# Revit family: RFll-TY3551_Imperial
name_source: partatom
category: Sprinklers
units: mm (PartAtom-declared; Revit-internal decimal feet)

## family parameters
Always vertical = Yes
Cut with Voids When Loaded = No
Maintain Annotation Orientation = No
OmniClass Number = 23.65.70.17.11.24
OmniClass Title = Fire Fighting Sprinkler Heads
Part Type = Normal
Room Calculation Point = No
Round Connector Dimension = Use Diameter
Shared = No
Work Plane-Based = No

## types (2) — shared parameters
COBie = Yes
COBie.Component.Name = Sprinklers:Concealed Flush
COBie.Type = Yes
COBie.Type.AssetType = Fixed
COBie.Type.Category = Pr_70_55_97_84:Sprinklers
COBie.Type.DurationUnit = year
COBie.Type.Finish = Bronze
COBie.Type.Manufacturer = Tyco Fire Protection Products
COBie.Type.Material = Bronze
COBie.Type.NominalHeight = 0' - 0"
COBie.Type.NominalLength = 0' - 0"
COBie.Type.NominalWidth = 0' - 0"
COBie.Type.Shape = Cylinder
COBie.Type.Size = 1/2"(DN15)
COBie.Type.WarrantyGuarantorParts = http://tycofsbp.com
Cover Plate Color = Tyco - White
Coverage = Standard
Coverage_ = Standard
Default Elevation = 0' - 0"
Finish_ = Natural Brass
K-Factor = 5.6
Manufacturer = Tyco Fire Protection Products
Manufacturer URL = www.tyco-fire.com
Material_ = Bronze
Model = RFII
Nominal Diameter 1 = 1"
Orifice = Extra Large
Orifice Size = 0"
Outside Diameter 1 = 1"
Response = Standard
Response_ = Standard
SIN No = TFP181
Takeout 1 = 2"
zero-valued in all types: COBie.Type.ReplacementCost, Style Id

## per-type parameters (varying)
| type | COBie.Component.Description | COBie.Type.ModelNumber | COBie.Type.ModelReference | Description | Part No | Technical Data Sheet No | Temperature Rating |
| RFll Concealed Pendent 1/2" NPT 155°F Brass_51-790-1-155 | RFII Concealed Flush SC SR 155°F K5.6 1/2 NPT | 51-790-1-155 | RFII Concealed Flush SC SR 155°F K5.6 1/2 NPT | Tyco RF II Pendent K5.6/80 155°F 1/2" NPT Brass Plated TY3551 | 51-790-1-155 | TFP3551 | 154 °F |
| RFll Concealed Pendent 1/2" NPT 200°F Brass_51-790-1-200 | RFII Concealed Flush SC SR 200°F K5.6 1/2 NPT | 51-790-1-200 | RFII Concealed Flush SC SR 200°F K5.6 1/2 NPT | Tyco RF II Pendent K5.6/80 200°F 1/2" NPT Brass Plated TY3551 | 51-790-1-200 | TY3551 | 199 °F |

## geometry (parser evidence)
native form markers: Blend x4, Sweep x30
no freeform markers — native parametric forms only
